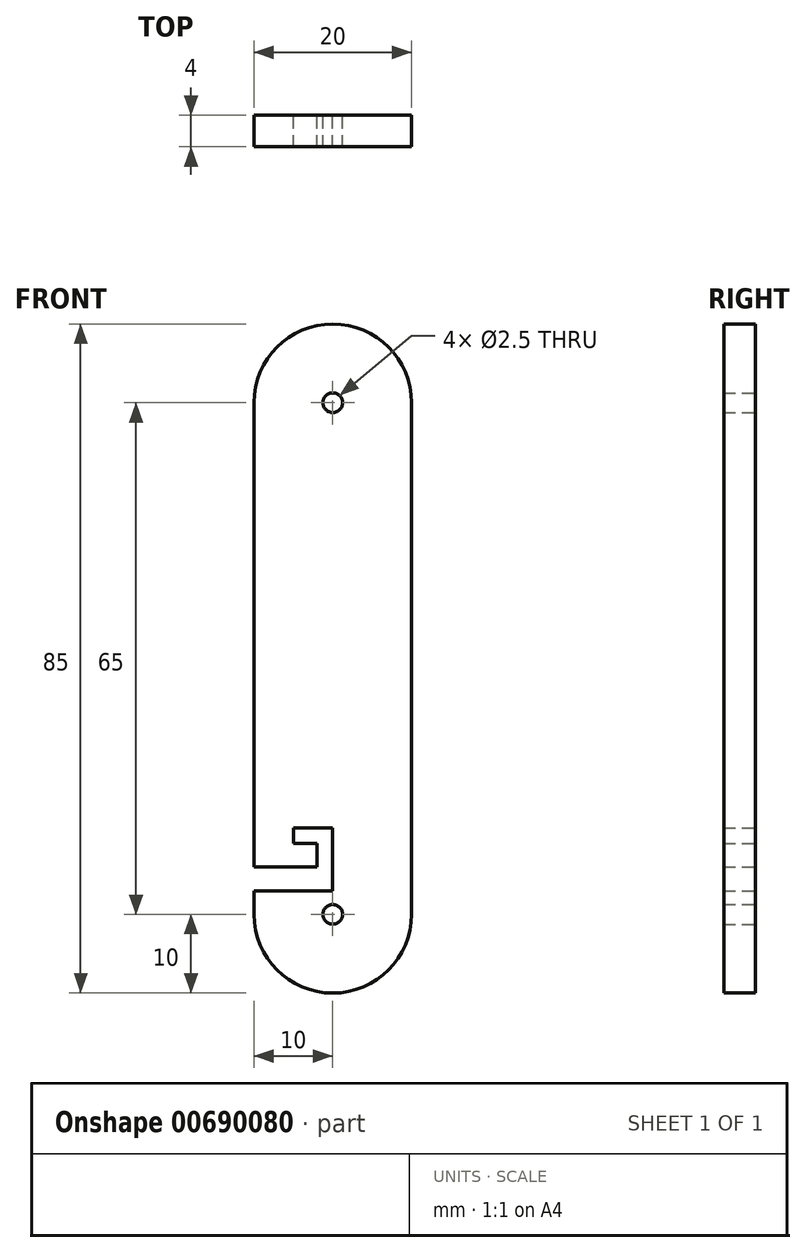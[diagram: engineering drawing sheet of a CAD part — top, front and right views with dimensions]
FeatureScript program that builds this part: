
annotation { "Feature Type Name" : "Feature", "Feature Type Description" : "" }
export const myFeature = defineFeature(function(context is Context, id is Id, definition is map)
    precondition{}
    {
        {
            var Q0;
            Q0=qCreatedBy(makeId("Front.planeOp"),FACE);
            var sketch = newSketch(context, id + "F0", { "sketchPlane" : qUnion([Q0])});
            skLineSegment(sketch, "E0", {"start": v(10, 65) * mm, "end": v(10, 0) * mm});
            skArc(sketch, "E1", {"start": v(-10, 0) * mm, "mid": v(0, -10) * mm, "end": v(10, 0) * mm});
            skLineSegment(sketch, "E2", {"start": v(-10, 0) * mm, "end": v(-10, 3) * mm});
            skLineSegment(sketch, "E3", {"start": v(-10, 6) * mm, "end": v(-10, 65) * mm});
            skLineSegment(sketch, "E4", {"start": v(-10, 65) * mm, "end": v(10, 65) * mm, "construction": true});
            skLineSegment(sketch, "E5", {"start": v(-10, 3) * mm, "end": v(0, 3) * mm});
            skLineSegment(sketch, "E6", {"start": v(0, 3) * mm, "end": v(0, 11) * mm});
            skLineSegment(sketch, "E7", {"start": v(0, 11) * mm, "end": v(-5, 11) * mm});
            skLineSegment(sketch, "E8", {"start": v(-5, 11) * mm, "end": v(-5, 9) * mm});
            skLineSegment(sketch, "E9", {"start": v(-5, 9) * mm, "end": v(-2, 9) * mm});
            skLineSegment(sketch, "E10", {"start": v(-2, 9) * mm, "end": v(-2, 6) * mm});
            skLineSegment(sketch, "E11", {"start": v(-2, 6) * mm, "end": v(-10, 6) * mm});
            skArc(sketch, "E12.MirrorCS", {"start": v(-10, 130) * mm, "mid": v(0, 140) * mm, "end": v(10, 130) * mm});
            skCircle(sketch, "E13", {"center": v(0, 65) * mm, "radius": 1.25 * mm});
            skCircle(sketch, "E14", {"center": v(0, 0) * mm, "radius": 1.25 * mm});
            skCircle(sketch, "E15.MirrorC", {"center": v(0, 130) * mm, "radius": 1.25 * mm});
            skArc(sketch, "E16", {"start": v(10, 65) * mm, "mid": v(0, 75) * mm, "end": v(-10, 65) * mm});
            skLineSegment(sketch, "E17", {"start": v(-10, 65) * mm, "end": v(-10, 130) * mm});
            skLineSegment(sketch, "E18", {"start": v(10, 65) * mm, "end": v(10, 124) * mm});
            skLineSegment(sketch, "E19", {"start": v(10, 130) * mm, "end": v(10, 127) * mm});
            skLineSegment(sketch, "E20", {"start": v(10, 127) * mm, "end": v(0, 127) * mm});
            skLineSegment(sketch, "E21", {"start": v(0, 127) * mm, "end": v(0, 119) * mm});
            skLineSegment(sketch, "E22", {"start": v(0, 119) * mm, "end": v(5, 119) * mm});
            skLineSegment(sketch, "E23", {"start": v(5, 119) * mm, "end": v(5, 121) * mm});
            skLineSegment(sketch, "E24", {"start": v(5, 121) * mm, "end": v(5, 121) * mm});
            skLineSegment(sketch, "E25", {"start": v(2, 121) * mm, "end": v(5, 121) * mm});
            skLineSegment(sketch, "E26", {"start": v(2, 121) * mm, "end": v(2, 124) * mm});
            skLineSegment(sketch, "E27", {"start": v(2, 124) * mm, "end": v(10, 124) * mm});
            skSolve(sketch);
        }
        {
            var Q0;
            Q0=makeQuery(id+"F0.imprint","IMPRINT",FACE,{"disambiguationData":[TD([[makeQuery(id+"F0.imprint","IMPRINT",EDGE,{"derivedFrom":sQuery(id+"F0.wireOp",EDGE,"E0")}),-1.0]])]});
            var Q1;
            Q1=makeQuery(id+"F0.imprint","IMPRINT",FACE,{"disambiguationData":[TD([[makeQuery(id+"F0.imprint","IMPRINT",EDGE,{"derivedFrom":sQuery(id+"F0.wireOp",EDGE,"E12.MirrorCS")}),-1.0]])]});
            extrude(context, id + "F1", {"entities" : qUnion([Q0, Q1]), "depth" : 4 * mm, "offsetDistance" : 25 * mm});
        }
        {
            var Q0;
            Q0=makeQuery(id+"F0.imprint","IMPRINT",FACE,{"disambiguationData":[TD([[makeQuery(id+"F0.imprint","IMPRINT",EDGE,{"derivedFrom":sQuery(id+"F0.wireOp",EDGE,"E0")}),-1.0]])]});
            var Q1;
            Q1=makeQuery(id+"F1.opExtrude","CAP_FACE",FACE,{"disambiguationData":[OSD([sQuery(id+"F0.wireOp",EDGE,"E0"),sQuery(id+"F0.wireOp",EDGE,"E1"),sQuery(id+"F0.wireOp",EDGE,"E2"),sQuery(id+"F0.wireOp",EDGE,"E3"),sQuery(id+"F0.wireOp",EDGE,"E5"),sQuery(id+"F0.wireOp",EDGE,"E6"),sQuery(id+"F0.wireOp",EDGE,"E7"),sQuery(id+"F0.wireOp",EDGE,"E8"),sQuery(id+"F0.wireOp",EDGE,"E9"),sQuery(id+"F0.wireOp",EDGE,"E10"),sQuery(id+"F0.wireOp",EDGE,"E11"),sQuery(id+"F0.wireOp",EDGE,"70ec269a-8ceb-4464-b00d-76321fb2717a0.MirrorCS"),sQuery(id+"F0.wireOp",EDGE,"E12.MirrorCS"),sQuery(id+"F0.wireOp",EDGE,"7d6ab145-71a7-4c0b-b8e7-2355f92b67640.MirrorCS"),sQuery(id+"F0.wireOp",EDGE,"c04f4631-8198-4f8b-9cf4-1913edc42f2d0.MirrorCS"),sQuery(id+"F0.wireOp",EDGE,"8f9a35b7-6a49-4e0c-95c4-d8f9d8de3f280.MirrorCS"),sQuery(id+"F0.wireOp",EDGE,"8809ebaf-2206-4ac5-8a1e-b355378c352c0.MirrorCS"),sQuery(id+"F0.wireOp",EDGE,"ad24100e-1e79-4c95-8a1a-d1b819d70de10.MirrorCS"),sQuery(id+"F0.wireOp",EDGE,"dfbd025f-9f43-4fea-b71c-fe9d3827b43c0.MirrorCS"),sQuery(id+"F0.wireOp",EDGE,"59e0db29-8706-48e4-ba2a-459ba78bf4690.MirrorCS"),sQuery(id+"F0.wireOp",EDGE,"5e7f0a4b-7dcf-4864-abe0-c09e0665589b0.MirrorCS"),sQuery(id+"F0.wireOp",EDGE,"E13"),sQuery(id+"F0.wireOp",EDGE,"E14"),sQuery(id+"F0.wireOp",EDGE,"36ee51b3-d411-422f-8a9b-4da323153ea40.MirrorCS"),sQuery(id+"F0.wireOp",EDGE,"E15.MirrorC")])],"isStart":false});
            extrude(context, id + "F2", {"entities" : qUnion([Q0]), "endBound" : BoundingType.UP_TO_SURFACE, "depth" : 25 * mm, "endBoundEntityFace" : qUnion([Q1]), "offsetDistance" : 25 * mm});
        }
    });
